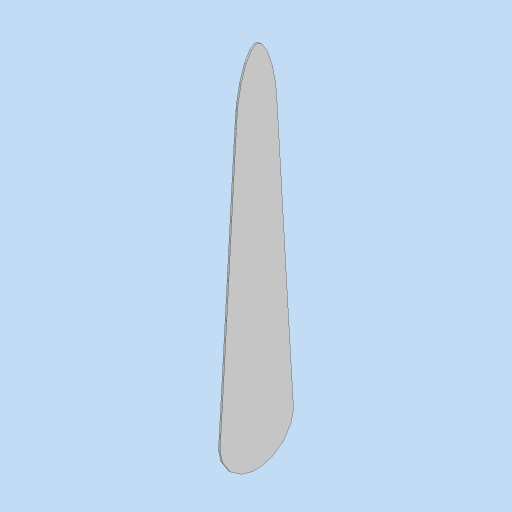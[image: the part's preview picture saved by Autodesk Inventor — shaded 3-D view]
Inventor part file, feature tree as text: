
AUTODESK INVENTOR PART (.ipt)
format: ipt  version: 2024 (Build 280153000, 153)  size: 238,080 bytes
history: native  units: mm
features: extrude x2, sketch x2
ambient origin geometry x8: Origin, YZ Plane, XZ Plane, XY Plane, X Axis, Y Axis, Z Axis, Center Point
bodies: Body1 (feature_tree)
feature tree (4):
  extrude  "Extrusion27"  Depth=0.25mm
  extrude  "Extrusion30"  Depth=10.0mm TaperAngle=0.0deg
  sketch  "Sketch1"  dims[d84=0.25mm d85=0.0mm d91=11.0mm]
  sketch  "Sketch7"  dims[d92=1.0mm d93=10.0mm d94=0.0mm d6=0.5mm d7=0.872665mm d8=0.5mm d9=0.872665mm]
